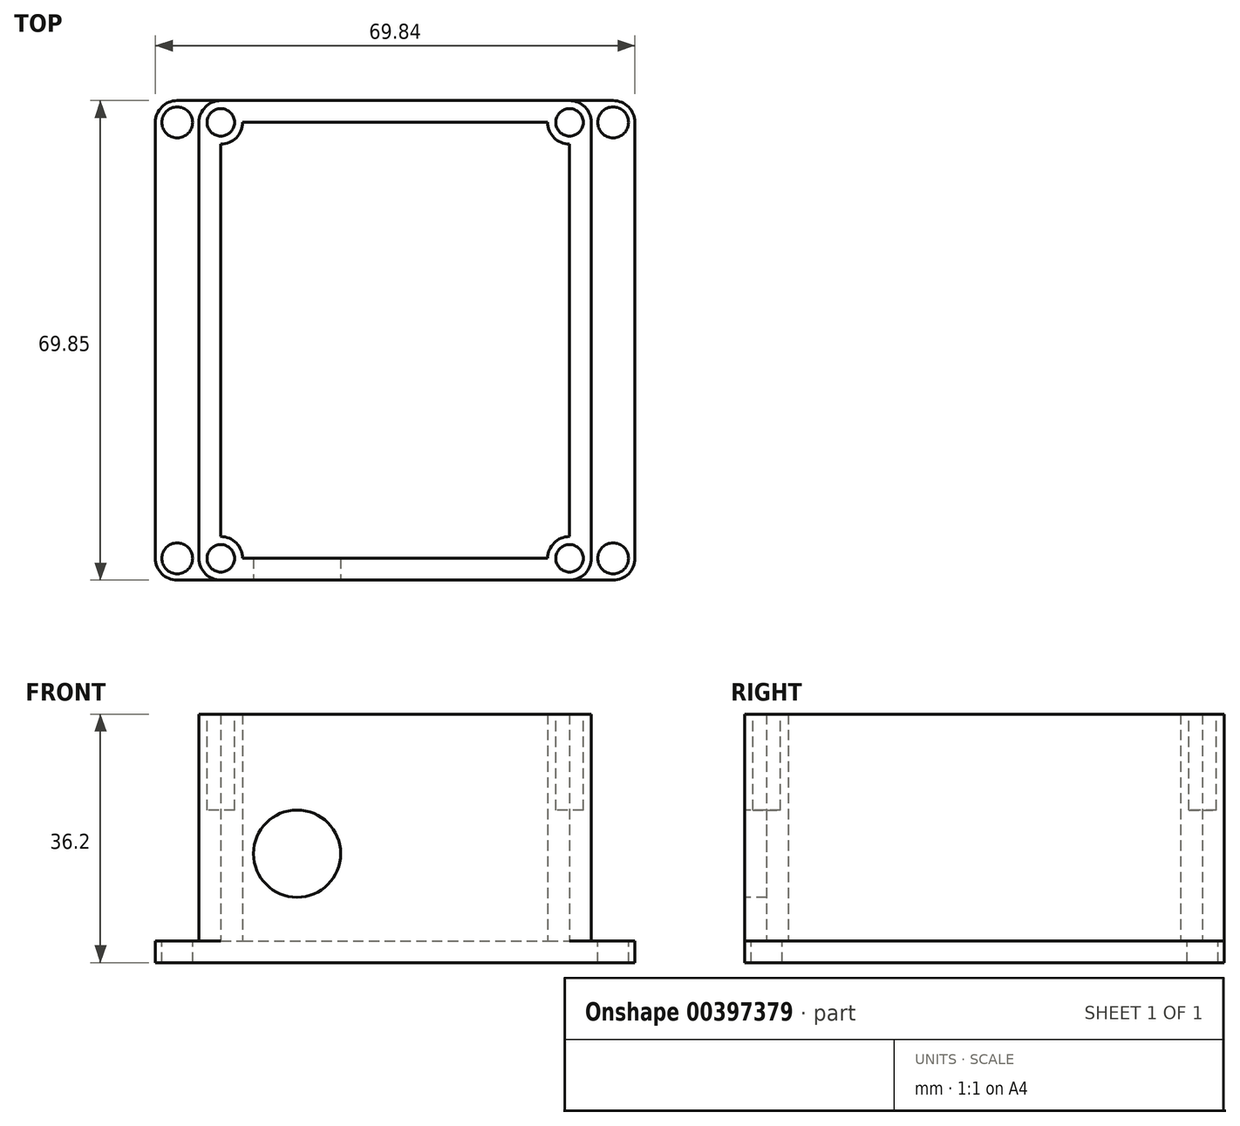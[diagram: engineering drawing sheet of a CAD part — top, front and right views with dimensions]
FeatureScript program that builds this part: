
annotation { "Feature Type Name" : "Feature", "Feature Type Description" : "" }
export const myFeature = defineFeature(function(context is Context, id is Id, definition is map)
    precondition{}
    {
        {
            var Q0;
            Q0=qCreatedBy(makeId("Top.planeOp"),FACE);
            var sketch = newSketch(context, id + "F0", { "sketchPlane" : qUnion([Q0])});
            skLineSegment(sketch, "E0.bottom", {"start": v(-34.93, 34.93) * mm, "end": v(34.93, 34.93) * mm});
            skLineSegment(sketch, "E0.top", {"start": v(-34.93, -34.93) * mm, "end": v(34.93, -34.93) * mm});
            skLineSegment(sketch, "E0.left", {"start": v(-34.93, 34.93) * mm, "end": v(-34.93, -34.93) * mm});
            skLineSegment(sketch, "E0.right", {"start": v(34.93, 34.93) * mm, "end": v(34.93, -34.93) * mm});
            skSolve(sketch);
        }
        {
            var Q0;
            Q0 = qSketchRegion(id + "F0", true);
            extrude(context, id + "F1", {"entities" : qUnion([Q0]), "depth" : 3.17 * mm});
        }
        {
            var Q0;
            Q0=makeQuery(id+"F1.opExtrude","SWEPT_EDGE",EDGE,{"disambiguationData":[OSD([sQuery(id+"F0.wireOp",EDGE,"E0.top"),sQuery(id+"F0.wireOp",EDGE,"E0.left")])]});
            var Q1;
            Q1=makeQuery(id+"F1.opExtrude","SWEPT_EDGE",EDGE,{"disambiguationData":[OSD([sQuery(id+"F0.wireOp",EDGE,"E0.top"),sQuery(id+"F0.wireOp",EDGE,"E0.right")])]});
            var Q2;
            Q2=makeQuery(id+"F1.opExtrude","SWEPT_EDGE",EDGE,{"disambiguationData":[OSD([sQuery(id+"F0.wireOp",EDGE,"E0.bottom"),sQuery(id+"F0.wireOp",EDGE,"E0.right")])]});
            var Q3;
            Q3=makeQuery(id+"F1.opExtrude","SWEPT_EDGE",EDGE,{"disambiguationData":[OSD([sQuery(id+"F0.wireOp",EDGE,"E0.bottom"),sQuery(id+"F0.wireOp",EDGE,"E0.left")])]});
            fillet(context, id + "F2", {"entities" : qUnion([Q0, Q1, Q2, Q3]), "radius" : 3.17 * mm, "tangentPropagation" : true, "allowEdgeOverflow" : false});
        }
        {
            var Q0;
            Q0=makeQuery(id+"F1.opExtrude","CAP_FACE",FACE,{"disambiguationData":[OSD([sQuery(id+"F0.wireOp",EDGE,"E0.bottom"),sQuery(id+"F0.wireOp",EDGE,"E0.top"),sQuery(id+"F0.wireOp",EDGE,"E0.left"),sQuery(id+"F0.wireOp",EDGE,"E0.right")])],"isStart":false});
            var sketch = newSketch(context, id + "F3", { "sketchPlane" : qUnion([Q0])});
            skCircle(sketch, "E1", {"center": v(-31.75, 31.75) * mm, "radius": 2.25 * mm});
            skCircle(sketch, "E2", {"center": v(31.75, 31.75) * mm, "radius": 2.25 * mm});
            skCircle(sketch, "E3", {"center": v(31.75, -31.75) * mm, "radius": 2.25 * mm});
            skCircle(sketch, "E4", {"center": v(-31.75, -31.75) * mm, "radius": 2.25 * mm});
            skSolve(sketch);
        }
        {
            var Q0;
            Q0 = qSketchRegion(id + "F3", true);
            extrude(context, id + "F4", {"entities" : qUnion([Q0]), "operationType" : NewBodyOperationType.REMOVE, "oppositeDirection" : true, "depth" : 25.4 * mm, "hasSecondDirection" : true, "secondDirectionBound" : SecondDirectionBoundingType.THROUGH_ALL, "secondDirectionOppositeDirection" : false, "secondDirectionDepth" : 25.4 * mm});
        }
        {
            var Q0;
            Q0=makeQuery(id+"F1.opExtrude","CAP_FACE",FACE,{"disambiguationData":[OSD([sQuery(id+"F0.wireOp",EDGE,"E0.bottom"),sQuery(id+"F0.wireOp",EDGE,"E0.top"),sQuery(id+"F0.wireOp",EDGE,"E0.left"),sQuery(id+"F0.wireOp",EDGE,"E0.right")])],"isStart":false});
            var sketch = newSketch(context, id + "F5", { "sketchPlane" : qUnion([Q0])});
            skLineSegment(sketch, "E5.bottom", {"start": v(-25.4, 34.93) * mm, "end": v(25.4, 34.93) * mm});
            skLineSegment(sketch, "E5.top", {"start": v(-25.4, -34.93) * mm, "end": v(25.4, -34.93) * mm});
            skLineSegment(sketch, "E5.left", {"start": v(-28.58, 31.75) * mm, "end": v(-28.58, -31.75) * mm});
            skLineSegment(sketch, "E5.right", {"start": v(28.57, 31.75) * mm, "end": v(28.58, -31.75) * mm});
            skLineSegment(sketch, "E6.bottom", {"start": v(-22.23, 31.75) * mm, "end": v(22.22, 31.75) * mm});
            skLineSegment(sketch, "E6.top", {"start": v(-22.23, -31.75) * mm, "end": v(22.23, -31.75) * mm});
            skLineSegment(sketch, "E6.left", {"start": v(-25.4, 28.57) * mm, "end": v(-25.4, -28.58) * mm});
            skLineSegment(sketch, "E6.right", {"start": v(25.4, 28.58) * mm, "end": v(25.4, -28.58) * mm});
            skPoint(sketch, "E7.visualSharp", {"position": v(-25.4, 31.75) * mm});
            skPoint(sketch, "E8.visualSharp", {"position": v(-28.58, 34.93) * mm});
            skPoint(sketch, "E9.visualSharp", {"position": v(-25.4, -31.75) * mm});
            skPoint(sketch, "E10.visualSharp", {"position": v(-28.58, -34.93) * mm});
            skPoint(sketch, "E11.visualSharp", {"position": v(28.58, -34.93) * mm});
            skPoint(sketch, "E12.visualSharp", {"position": v(25.4, -31.75) * mm});
            skPoint(sketch, "E13.visualSharp", {"position": v(25.4, 31.75) * mm});
            skPoint(sketch, "E14.visualSharp", {"position": v(28.57, 34.93) * mm});
            skArc(sketch, "E15", {"start": v(-25.4, 28.57) * mm, "mid": v(-23.15, 29.5) * mm, "end": v(-22.23, 31.75) * mm});
            skArc(sketch, "E16.trimOffspring", {"start": v(-25.4, 34.92) * mm, "mid": v(-27.65, 34) * mm, "end": v(-28.58, 31.75) * mm});
            skArc(sketch, "E17", {"start": v(22.22, 31.75) * mm, "mid": v(23.15, 29.5) * mm, "end": v(25.4, 28.58) * mm});
            skArc(sketch, "E18.trimOffspring", {"start": v(28.57, 31.75) * mm, "mid": v(27.65, 34) * mm, "end": v(25.4, 34.93) * mm});
            skArc(sketch, "E19", {"start": v(-28.58, -31.75) * mm, "mid": v(-27.65, -34) * mm, "end": v(-25.4, -34.93) * mm});
            skArc(sketch, "E20.trimOffspring", {"start": v(-22.23, -31.75) * mm, "mid": v(-23.15, -29.5) * mm, "end": v(-25.4, -28.58) * mm});
            skArc(sketch, "E21", {"start": v(25.4, -28.58) * mm, "mid": v(23.15, -29.5) * mm, "end": v(22.23, -31.75) * mm});
            skArc(sketch, "E22.trimOffspring", {"start": v(25.4, -34.93) * mm, "mid": v(27.65, -34) * mm, "end": v(28.58, -31.75) * mm});
            skSolve(sketch);
        }
        {
            var Q0;
            Q0 = qSketchRegion(id + "F5", true);
            extrude(context, id + "F6", {"entities" : qUnion([Q0]), "operationType" : NewBodyOperationType.ADD, "depth" : 25.4 * mm});
        }
        {
            var Q0;
            Q0=makeQuery(id+"F6.opExtrude","CAP_FACE",FACE,{"disambiguationData":[OSD([sQuery(id+"F5.wireOp",EDGE,"E5.bottom"),sQuery(id+"F5.wireOp",EDGE,"E5.top"),sQuery(id+"F5.wireOp",EDGE,"E5.left"),sQuery(id+"F5.wireOp",EDGE,"E5.right"),sQuery(id+"F5.wireOp",EDGE,"E6.bottom"),sQuery(id+"F5.wireOp",EDGE,"E6.top"),sQuery(id+"F5.wireOp",EDGE,"E6.left"),sQuery(id+"F5.wireOp",EDGE,"E6.right"),sQuery(id+"F5.wireOp",EDGE,"E15"),sQuery(id+"F5.wireOp",EDGE,"E16.trimOffspring"),sQuery(id+"F5.wireOp",EDGE,"E17"),sQuery(id+"F5.wireOp",EDGE,"E18.trimOffspring"),sQuery(id+"F5.wireOp",EDGE,"E19"),sQuery(id+"F5.wireOp",EDGE,"E20.trimOffspring"),sQuery(id+"F5.wireOp",EDGE,"E21"),sQuery(id+"F5.wireOp",EDGE,"E22.trimOffspring")])],"isStart":false});
            var sketch = newSketch(context, id + "F7", { "sketchPlane" : qUnion([Q0])});
            skCircle(sketch, "E23", {"center": v(-25.4, 31.75) * mm, "radius": 2 * mm});
            skCircle(sketch, "E24", {"center": v(25.4, 31.75) * mm, "radius": 2 * mm});
            skCircle(sketch, "E25", {"center": v(25.4, -31.75) * mm, "radius": 2 * mm});
            skCircle(sketch, "E26", {"center": v(-25.4, -31.75) * mm, "radius": 2 * mm});
            skSolve(sketch);
        }
        {
            var Q0;
            Q0 = qSketchRegion(id + "F7", true);
            extrude(context, id + "F8", {"entities" : qUnion([Q0]), "operationType" : NewBodyOperationType.REMOVE, "oppositeDirection" : true, "depth" : 6.35 * mm});
        }
        {
            var Q0;
            Q0=makeQuery(id+"F6.boolean.opBoolean","MERGE",FACE,{"derivedFrom":[makeQuery(id+"F1.opExtrude","SWEPT_FACE",FACE,{"disambiguationData":[OSD([sQuery(id+"F0.wireOp",EDGE,"E0.top")])]}),makeQuery(id+"F6.opExtrude","SWEPT_FACE",FACE,{"disambiguationData":[OSD([sQuery(id+"F5.wireOp",EDGE,"E5.top")])]})]});
            var sketch = newSketch(context, id + "F9", { "sketchPlane" : qUnion([Q0])});
            skCircle(sketch, "E27", {"center": v(-14.29, 15.88) * mm, "radius": 6.35 * mm});
            skSolve(sketch);
        }
        {
            var Q0;
            Q0 = qSketchRegion(id + "F9", true);
            extrude(context, id + "F10", {"entities" : qUnion([Q0]), "operationType" : NewBodyOperationType.REMOVE, "endBound" : BoundingType.UP_TO_NEXT, "oppositeDirection" : true, "depth" : 25.4 * mm});
        }
        {
            var Q0;
            Q0=makeQuery(id+"F6.opExtrude","CAP_FACE",FACE,{"disambiguationData":[OSD([sQuery(id+"F5.wireOp",EDGE,"E5.bottom"),sQuery(id+"F5.wireOp",EDGE,"E5.top"),sQuery(id+"F5.wireOp",EDGE,"E5.left"),sQuery(id+"F5.wireOp",EDGE,"E5.right"),sQuery(id+"F5.wireOp",EDGE,"E6.bottom"),sQuery(id+"F5.wireOp",EDGE,"E6.top"),sQuery(id+"F5.wireOp",EDGE,"E6.left"),sQuery(id+"F5.wireOp",EDGE,"E6.right"),sQuery(id+"F5.wireOp",EDGE,"E15"),sQuery(id+"F5.wireOp",EDGE,"E16.trimOffspring"),sQuery(id+"F5.wireOp",EDGE,"E17"),sQuery(id+"F5.wireOp",EDGE,"E18.trimOffspring"),sQuery(id+"F5.wireOp",EDGE,"E19"),sQuery(id+"F5.wireOp",EDGE,"E20.trimOffspring"),sQuery(id+"F5.wireOp",EDGE,"E21"),sQuery(id+"F5.wireOp",EDGE,"E22.trimOffspring")])],"isStart":false});
            extrude(context, id + "F11", {"entities" : qUnion([Q0]), "operationType" : NewBodyOperationType.ADD, "depth" : 7.62 * mm, "offsetDistance" : 25.4 * mm});
        }
    });
